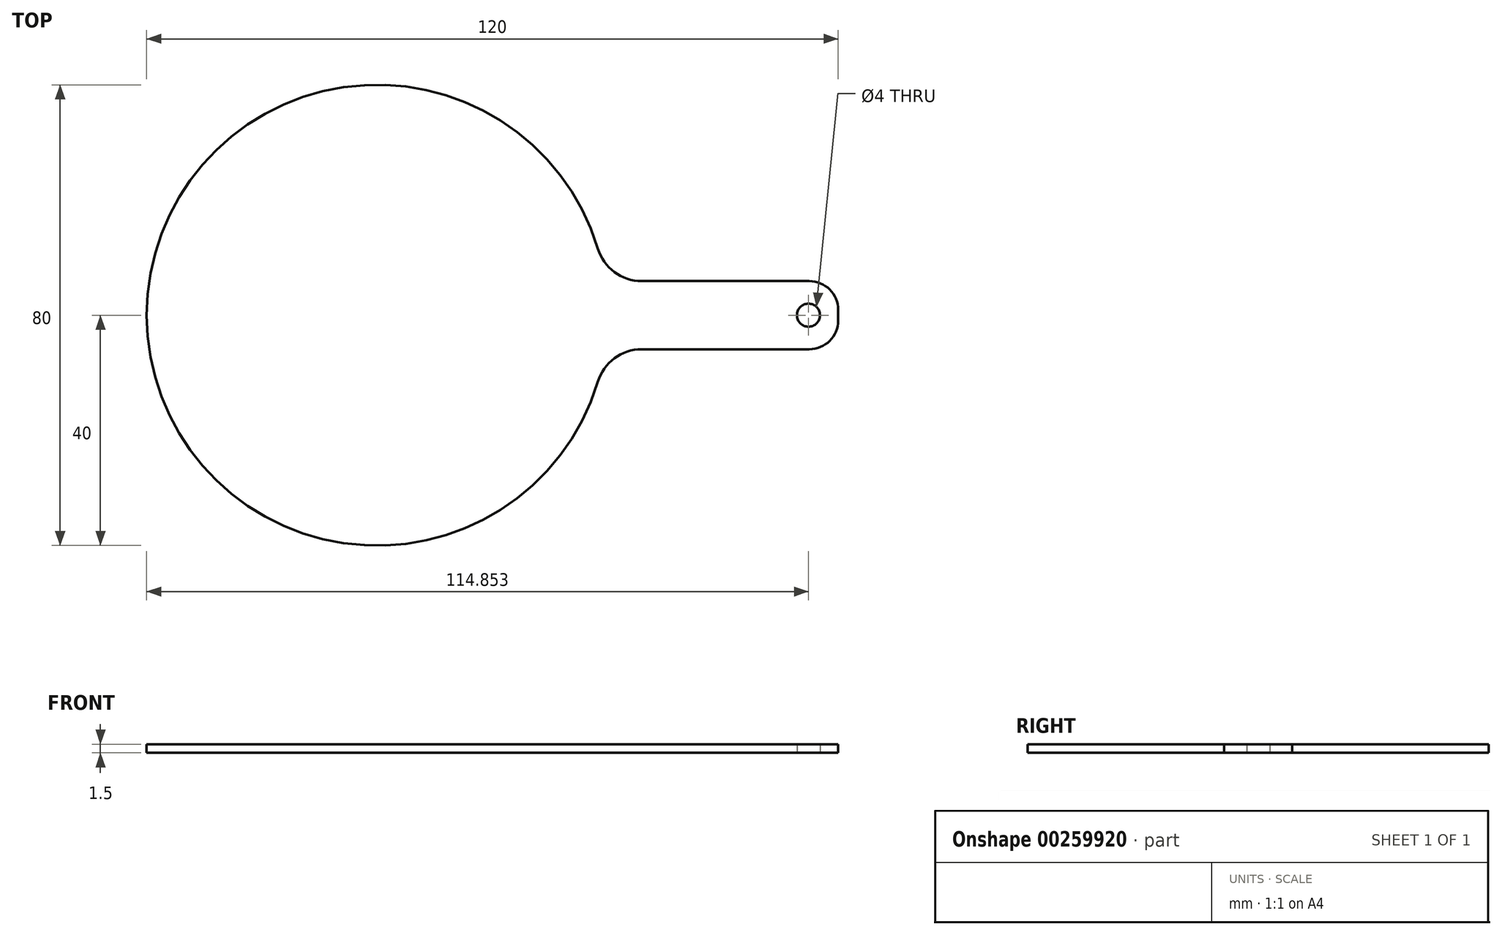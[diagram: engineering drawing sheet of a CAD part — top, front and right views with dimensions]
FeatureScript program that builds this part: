
annotation { "Feature Type Name" : "Feature", "Feature Type Description" : "" }
export const myFeature = defineFeature(function(context is Context, id is Id, definition is map)
    precondition{}
    {
        {
            var Q0;
            Q0=qCreatedBy(makeId("Top.planeOp"),FACE);
            var sketch = newSketch(context, id + "F0", { "sketchPlane" : qUnion([Q0])});
            skArc(sketch, "E0", {"start": v(38.28, 11.6) * mm, "mid": v(-40, 0) * mm, "end": v(38.28, -11.6) * mm});
            skLineSegment(sketch, "E1.bottom", {"start": v(75, 5.91) * mm, "end": v(45.94, 5.91) * mm});
            skLineSegment(sketch, "E1.top", {"start": v(75, -5.91) * mm, "end": v(45.94, -5.91) * mm});
            skLineSegment(sketch, "E1.left", {"start": v(80, 0.91) * mm, "end": v(80, -0.91) * mm});
            skPoint(sketch, "E1.middle", {"position": v(43.4, 0) * mm});
            skPoint(sketch, "E1.right.end.orphan", {"position": v(6.82, -5.91) * mm});
            skPoint(sketch, "E1.right.start.orphan", {"position": v(6.82, 5.91) * mm});
            skPoint(sketch, "E2.visualSharp", {"position": v(39.56, 5.91) * mm});
            skArc(sketch, "E2.filletArc", {"start": v(38.28, 11.6) * mm, "mid": v(41.17, 7.49) * mm, "end": v(45.94, 5.91) * mm});
            skPoint(sketch, "E3.visualSharp", {"position": v(39.56, -5.91) * mm});
            skArc(sketch, "E3.filletArc", {"start": v(45.94, -5.91) * mm, "mid": v(41.17, -7.49) * mm, "end": v(38.28, -11.6) * mm});
            skPoint(sketch, "E4.visualSharp", {"position": v(80, 5.91) * mm});
            skArc(sketch, "E4.filletArc", {"start": v(80, 0.91) * mm, "mid": v(78.54, 4.45) * mm, "end": v(75, 5.91) * mm});
            skPoint(sketch, "E5.visualSharp", {"position": v(80, -5.91) * mm});
            skArc(sketch, "E5.filletArc", {"start": v(75, -5.91) * mm, "mid": v(78.54, -4.45) * mm, "end": v(80, -0.91) * mm});
            skCircle(sketch, "E6", {"center": v(74.85, 0) * mm, "radius": 2 * mm});
            skSolve(sketch);
        }
        {
            var Q0;
            Q0 = qSketchRegion(id + "F0", true);
            extrude(context, id + "F1", {"entities" : qUnion([Q0]), "depth" : 1.5 * mm});
        }
    });
